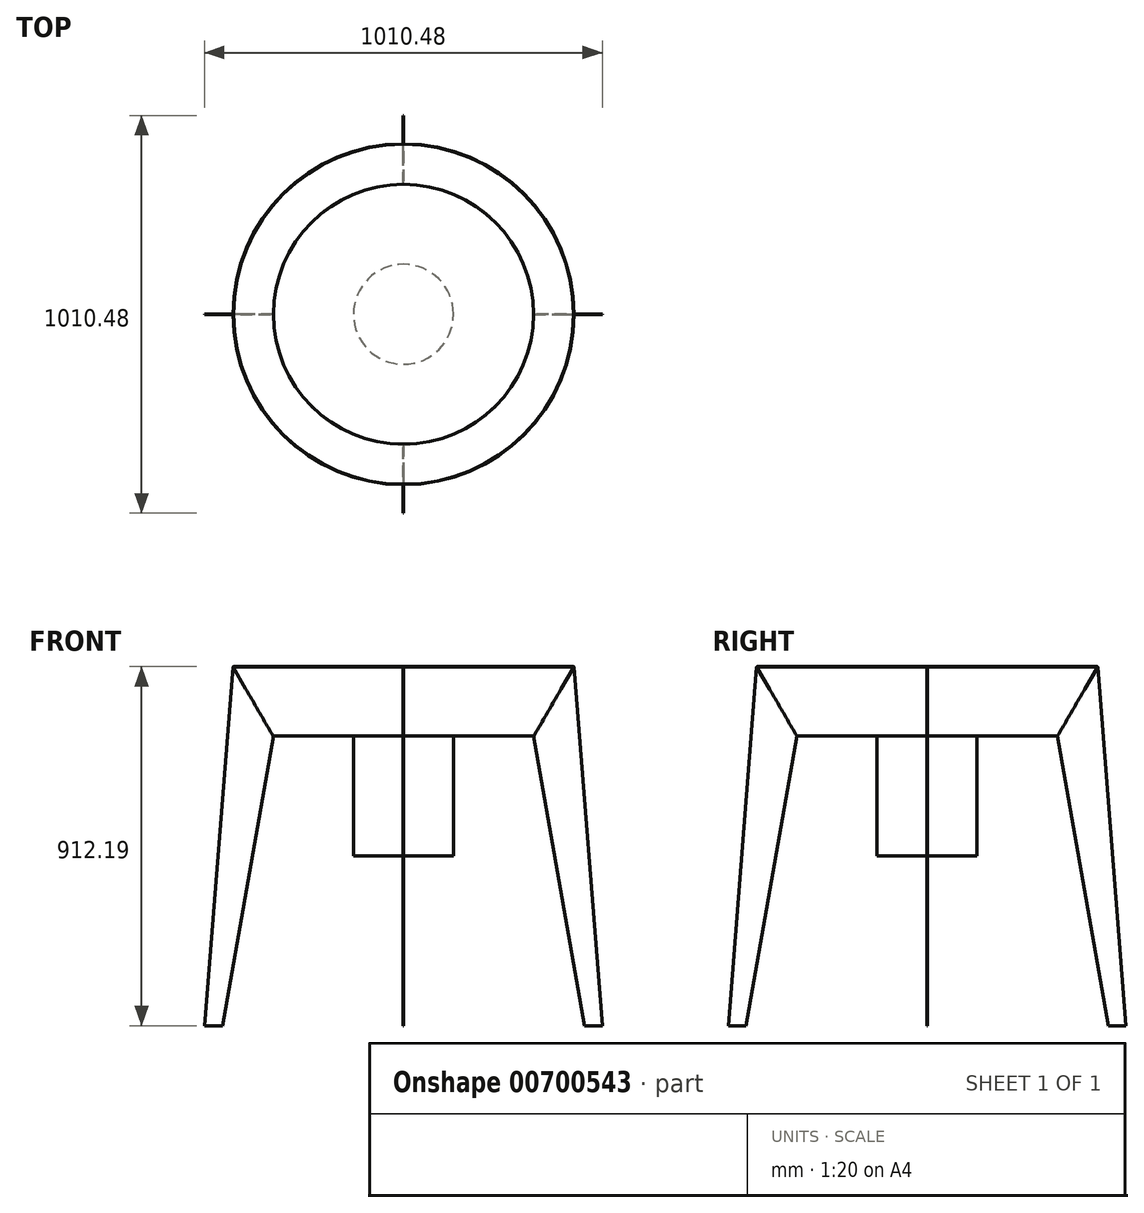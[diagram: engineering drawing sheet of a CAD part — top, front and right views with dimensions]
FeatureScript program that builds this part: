
annotation { "Feature Type Name" : "Feature", "Feature Type Description" : "" }
export const myFeature = defineFeature(function(context is Context, id is Id, definition is map)
    precondition{}
    {
        {
            var Q0;
            Q0=qCreatedBy(makeId("Front.planeOp"),FACE);
            var sketch = newSketch(context, id + "F0", { "sketchPlane" : qUnion([Q0])});
            skLineSegment(sketch, "E0", {"start": v(0, 0) * mm, "end": v(-101.6, 175.98) * mm});
            skLineSegment(sketch, "E1.0", {"start": v(-1.05, -0.6) * mm, "end": v(-102.65, 175.37) * mm});
            skLineSegment(sketch, "E2", {"start": v(-101.6, 175.98) * mm, "end": v(-102.65, 175.37) * mm});
            skLineSegment(sketch, "E3", {"start": v(0, 0) * mm, "end": v(-1.05, -0.6) * mm});
            skSolve(sketch);
        }
        {
            var Q0;
            Q0=qCreatedBy(makeId("Right.planeOp"),FACE);
            cPlane(context, id + "F1", {"entities" : qUnion([Q0]), "cplaneType" : CPlaneType.OFFSET, "offset" : 330.2 * mm, "width" : 152.4 * mm, "height" : 152.4 * mm});
        }
        {
            var Q0;
            Q0=qCreatedBy(id+"F1.planeOp",FACE);
            var sketch = newSketch(context, id + "F2", { "sketchPlane" : qUnion([Q0])});
            skLineSegment(sketch, "E4", {"start": v(0, 0) * mm, "end": v(0, 101.47) * mm, "construction": true});
            skSolve(sketch);
        }
        {
            var Q0;
            Q0=makeQuery(id+"F0.imprint","IMPRINT",FACE,{"disambiguationData":[TD([[makeQuery(id+"F0.imprint","IMPRINT",EDGE,{"derivedFrom":sQuery(id+"F0.wireOp",EDGE,"E0")}),1.0]])]});
            var Q1;
            Q1=sQuery(id+"F2.wireOp",EDGE,"E4");
            revolve(context, id + "F3", {"entities" : qUnion([Q0]), "axis" : qUnion([Q1]), "revolveType" : RevolveType.FULL});
        }
        {
            var Q0;
            Q0=qCreatedBy(makeId("Right.planeOp"),FACE);
            cPlane(context, id + "F4", {"entities" : qUnion([Q0]), "cplaneType" : CPlaneType.OFFSET, "offset" : 101.6 * mm, "oppositeDirection" : true, "width" : 152.4 * mm, "height" : 152.4 * mm});
        }
        {
            var Q0;
            Q0=qCreatedBy(makeId("Front.planeOp"),FACE);
            var sketch = newSketch(context, id + "F5", { "sketchPlane" : qUnion([Q0])});
            skLineSegment(sketch, "E5", {"start": v(0, 0) * mm, "end": v(-103.3, 175.37) * mm});
            skLineSegment(sketch, "E6", {"start": v(-103.3, 175.37) * mm, "end": v(-175.04, -736.21) * mm});
            skLineSegment(sketch, "E7", {"start": v(-175.04, -736.21) * mm, "end": v(-129.81, -736.21) * mm});
            skLineSegment(sketch, "E8", {"start": v(-129.81, -736.21) * mm, "end": v(0, 0) * mm});
            skSolve(sketch);
        }
        {
            var Q0;
            Q0=makeQuery(id+"F5.imprint","IMPRINT",FACE,{"disambiguationData":[TD([[makeQuery(id+"F5.imprint","IMPRINT",EDGE,{"derivedFrom":sQuery(id+"F5.wireOp",EDGE,"E5")}),1.0]])]});
            extrude(context, id + "F6", {"entities" : qUnion([Q0]), "operationType" : NewBodyOperationType.ADD, "endBound" : BoundingType.SYMMETRIC, "depth" : 1.21 * mm, "offsetDistance" : 25.4 * mm});
        }
        {
            var Q0;
            Q0=makeQuery(id+"F3.opRevolve","SWEPT_BODY",BODY,{"disambiguationData":[OSD([sQuery(id+"F0.wireOp",EDGE,"E0"),sQuery(id+"F0.wireOp",EDGE,"E1.0"),sQuery(id+"F0.wireOp",EDGE,"E2"),sQuery(id+"F0.wireOp",EDGE,"E3")])]});
            var Q1;
            Q1=sQuery(id+"F2.wireOp",EDGE,"E4");
            circularPattern(context, id + "F7", {"entities" : qUnion([Q0]), "axis" : qUnion([Q1]), "angle" : 360 * degree, "instanceCount" : 4, "equalSpace" : true});
        }
        {
            var Q0;
            Q0=qCreatedBy(makeId("Top.planeOp"),FACE);
            var sketch = newSketch(context, id + "F8", { "sketchPlane" : qUnion([Q0])});
            skCircle(sketch, "E9", {"center": v(330.2, 0) * mm, "radius": 330.2 * mm});
            skSolve(sketch);
        }
        {
            var Q0;
            Q0=makeQuery(id+"F8.imprint","IMPRINT",FACE,{"disambiguationData":[TD([[makeQuery(id+"F8.imprint","IMPRINT",EDGE,{"derivedFrom":sQuery(id+"F8.wireOp",EDGE,"E9")}),1.0]])]});
            extrude(context, id + "F9", {"entities" : qUnion([Q0]), "depth" : 1.21 * mm, "offsetDistance" : 25.4 * mm});
        }
        {
            var Q0;
            Q0=qCreatedBy(makeId("Top.planeOp"),FACE);
            var sketch = newSketch(context, id + "F10", { "sketchPlane" : qUnion([Q0])});
            skCircle(sketch, "E10", {"center": v(330.2, 0) * mm, "radius": 127 * mm});
            skSolve(sketch);
        }
        {
            var Q0;
            Q0=makeQuery(id+"F10.imprint","IMPRINT",FACE,{"disambiguationData":[TD([[makeQuery(id+"F10.imprint","IMPRINT",EDGE,{"derivedFrom":sQuery(id+"F10.wireOp",EDGE,"E10")}),1.0]])]});
            extrude(context, id + "F11", {"entities" : qUnion([Q0]), "operationType" : NewBodyOperationType.ADD, "oppositeDirection" : true, "depth" : 304.8 * mm, "offsetDistance" : 25.4 * mm});
        }
    });
